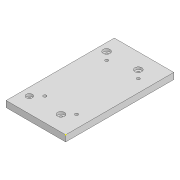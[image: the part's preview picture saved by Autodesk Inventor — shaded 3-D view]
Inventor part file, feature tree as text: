
AUTODESK INVENTOR PART (.ipt)
format: ipt  version: 2020 (Build 240168000, 168)  size: 183,808 bytes
history: native  units: mm
features: sketch x5, extrude x4, other x1
ambient origin geometry x8: Origin, YZ Plane, XZ Plane, XY Plane, X Axis, Y Axis, Z Axis, Center Point
bodies: Body1 (feature_tree)
feature tree (10):
  other  "Sólido1"
  extrude  "Extrusão1"  Depth=140.0mm
  extrude  "Extrusão2"  Depth=4.0mm
  sketch  "Esboço3"  dims[d4=4.0mm d5=4.0mm]
  extrude  "Extrusão3"  Depth=4.0mm
  extrude  "Extrusão4"  Depth=10.0mm
  sketch  "Esboço1"  dims[d0=77.0mm d1=140.0mm]
  sketch  "Esboço2"  dims[d2=4.0mm d3=4.0mm]
  sketch  "Esboço4"  dims[d6=10.0mm d7=10.0mm]
  sketch  "Esboço5"  dims[d8=20.0mm d9=20.0mm d10=20.0mm d11=20.0mm d12=26.0mm d13=26.0mm d14=8.0mm d15=0.0mm d16=8.0mm d17=9.0mm d18=9.0mm d19=9.0mm d20=3.0mm d21=0.0mm d22=4.0mm d23=4.0mm d24=10.0mm d25=10.0mm d26=10.0mm d27=10.0mm d28=4.0mm d29=4.0mm d30=10.0mm d31=10.0mm d32=10.0mm d33=10.0mm d34=12.0mm d35=0.0mm d36=8.0mm d37=8.0mm d38=8.0mm d39=8.0mm d40=5.0mm d41=0.0mm]
